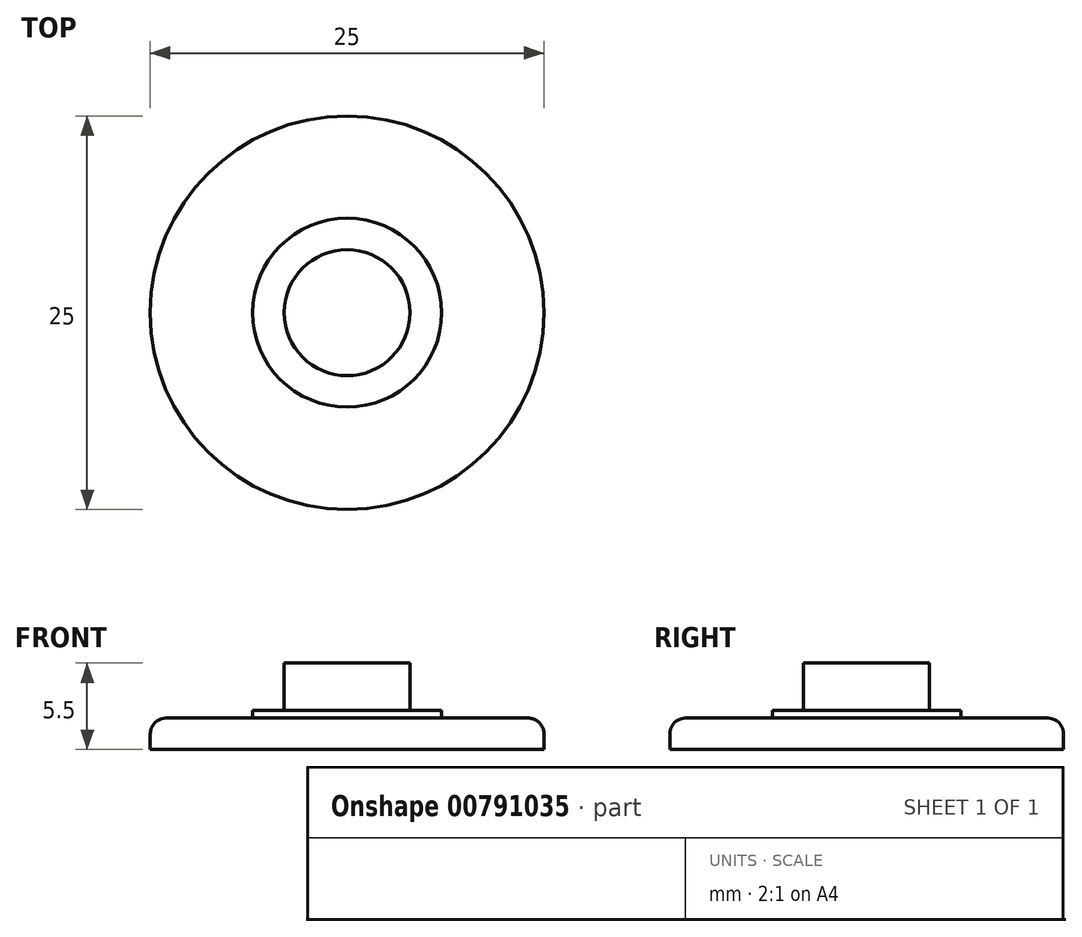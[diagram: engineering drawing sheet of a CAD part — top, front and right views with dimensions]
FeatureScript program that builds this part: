
annotation { "Feature Type Name" : "Feature", "Feature Type Description" : "" }
export const myFeature = defineFeature(function(context is Context, id is Id, definition is map)
    precondition{}
    {
        {
            var Q0;
            Q0=qCreatedBy(makeId("Top.planeOp"),FACE);
            var sketch = newSketch(context, id + "F0", { "sketchPlane" : qUnion([Q0])});
            skCircle(sketch, "E0", {"center": v(0, 0) * mm, "radius": 12.5 * mm});
            skSolve(sketch);
        }
        {
            var Q0;
            Q0=qSketchRegion(id+"F0",true);
            extrude(context, id + "F1", {"entities" : qUnion([Q0]), "depth" : 2 * mm, "offsetDistance" : 25 * mm});
        }
        {
            var Q0;
            Q0=makeQuery(id+"F1.opExtrude","CAP_EDGE",EDGE,{"disambiguationData":[OSD([sQuery(id+"F0.wireOp",EDGE,"E0")])],"isStart":false});
            fillet(context, id + "F2", {"entities" : qUnion([Q0]), "radius" : 1 * mm, "tangentPropagation" : true, "allowEdgeOverflow" : false});
        }
        {
            var Q0;
            Q0=makeQuery(id+"F1.opExtrude","CAP_FACE",FACE,{"disambiguationData":[OSD([sQuery(id+"F0.wireOp",EDGE,"E0")])],"isStart":false});
            var sketch = newSketch(context, id + "F3", { "sketchPlane" : qUnion([Q0])});
            skCircle(sketch, "E1", {"center": v(0, 0) * mm, "radius": 6 * mm});
            skSolve(sketch);
        }
        {
            var Q0;
            Q0=qSketchRegion(id+"F3",true);
            extrude(context, id + "F4", {"entities" : qUnion([Q0]), "operationType" : NewBodyOperationType.ADD, "depth" : 0.5 * mm, "offsetDistance" : 25 * mm});
        }
        {
            var Q0;
            Q0=makeQuery(id+"F4.opExtrude","CAP_FACE",FACE,{"disambiguationData":[OSD([sQuery(id+"F3.wireOp",EDGE,"E1")])],"isStart":false});
            var sketch = newSketch(context, id + "F5", { "sketchPlane" : qUnion([Q0])});
            skCircle(sketch, "E2", {"center": v(0, 0) * mm, "radius": 4 * mm});
            skSolve(sketch);
        }
        {
            var Q0;
            Q0=makeQuery(id+"F5.imprint","IMPRINT",FACE,{"disambiguationData":[TD([[makeQuery(id+"F5.imprint","IMPRINT",EDGE,{"derivedFrom":sQuery(id+"F5.wireOp",EDGE,"E2")}),1.0]])]});
            extrude(context, id + "F6", {"entities" : qUnion([Q0]), "operationType" : NewBodyOperationType.ADD, "depth" : 3 * mm, "offsetDistance" : 25 * mm});
        }
    });
